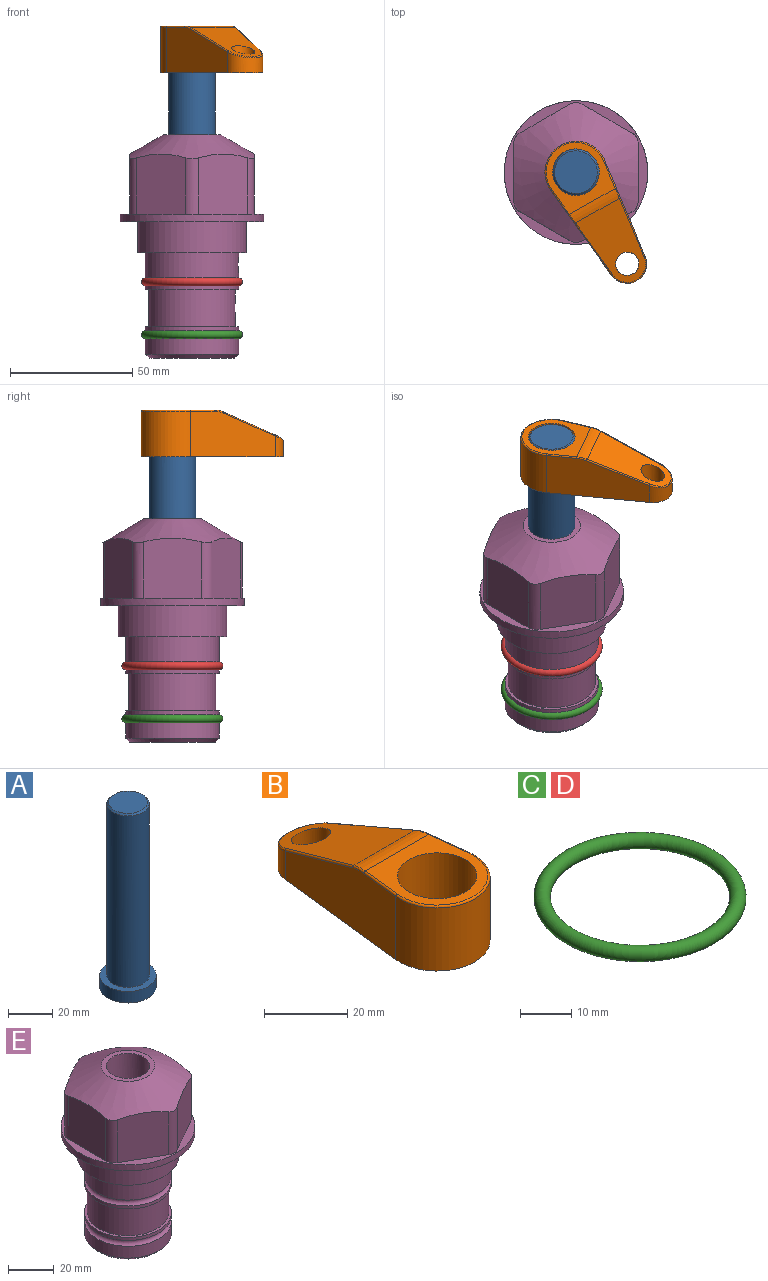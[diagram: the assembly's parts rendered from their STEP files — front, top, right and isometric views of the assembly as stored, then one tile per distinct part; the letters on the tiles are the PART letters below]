
ASSEMBLY  parts=5 mates=3
PART A: 6 faces, bbox 25.4x25.4x101.6 mm
  f0: plane 17.46x17.46mm, normal (0,0,1), area 239.5mm2, adj f5
  f1: plane 25.4x25.4mm, normal (0,0,-1), area 506.7mm2, adj f2
  f2: cylinder r=12.7mm len=25.4mm, axis (0,0,1), area 506.7mm2, adj f1,f3
  f3: plane 25.4x25.4mm, normal (0,0,1), area 221.7mm2, adj f2,f4
  f4: cylinder r=9.53mm len=94.46mm, axis (0,0,1), area 5653mm2, adj f3,f5
  f5: cone r=8.73mm half-angle=45deg, axis (0,0,-1), area 64.4mm2, adj f0,f4
PART B: 44 faces, bbox 27.5x64.5x19.1 mm
  f0: plane 2.3x0.95mm, normal (0,0,-1), area 1mm2, adj f25,f30,f34
  f1: plane 63.5x25.4mm, normal (0,0,-1), area 561.7mm2, adj f2,f3,f4,f5,f6,f7,f19,f20
  f2: cylinder r=12.7mm len=25.4mm, axis (0,0,-1), area 792.2mm2, adj f1,f3,f5,f13
  f3: plane 42.33x18.54mm, normal (0.99,0.11,0), area 647mm2, adj f1,f2,f4,f11,f12,f14
  f4: cylinder r=7.94mm len=15.78mm, axis (0,0,-1), area 158.6mm2, adj f1,f3,f5,f16
  f5: plane 42.33x18.54mm, normal (-0.99,0.11,0), area 647mm2, adj f1,f2,f4,f15,f17,f18
  f6: cylinder r=9.53mm len=19.05mm, axis (0,0,-1), area 1140.1mm2, adj f1,f8
  f7: cylinder r=4.76mm len=10.98mm, axis (0,0,-1), area 276.1mm2, adj f1,f9
  f8: plane 25.83x24.38mm, normal (0,0,1), area 262.2mm2, adj f6,f10,f11,f13,f15
  f9: plane 32.49x20.55mm, normal (0,0.34,0.94), area 489.9mm2, adj f7,f10,f14,f16,f18
  f10: cylinder r=12.7mm len=21.49mm, axis (-1,0,0), area 93.2mm2, adj f8,f9,f12,f17
  f11: cylinder r=0.51mm len=12.34mm, axis (0.11,-0.99,0), area 9.9mm2, adj f3,f8,f12,f13
  f12: bspline ~7.62x1.64mm, area 3.5mm2, adj f3,f10,f11,f14
  f13: torus R=12.19mm, axis (0,0,1), area 33.6mm2, adj f2,f8,f11,f15
  f14: cylinder r=0.51mm len=26.01mm, axis (0.1,-0.93,0.34), area 21.6mm2, adj f3,f9,f12,f16
  f15: cylinder r=0.51mm len=12.34mm, axis (0.11,0.99,0), area 9.9mm2, adj f5,f8,f13,f17
  f16: bspline ~15.78x7.05mm, area 15.7mm2, adj f4,f9,f14,f18
  f17: bspline ~7.62x1.64mm, area 3.5mm2, adj f5,f10,f15,f18
  f18: cylinder r=0.51mm len=26.01mm, axis (0.1,0.93,-0.34), area 21.6mm2, adj f5,f9,f16,f17
  f19: plane 21.6x14.29mm, normal (-0.99,-0.11,0), area 242.6mm2, adj f1,f26,f28,f34,f36,f38
  f20: plane 21.6x14.29mm, normal (0.99,-0.11,0), area 242.6mm2, adj f1,f27,f29,f37,f39,f41
  f21: cylinder r=12.7mm len=14.29mm, axis (0,0,-1), area 173.2mm2, adj f1,f26,f27,f30,f31,f33
  f22: cylinder r=7.94mm len=7.63mm, axis (0,0,-1), area 53.8mm2, adj f1,f28,f29,f42
  f23: plane 2.3x0.95mm, normal (0,0,-1), area 1mm2, adj f25,f33,f37
  f24: plane 17.94x12.32mm, normal (0,-0.34,-0.94), area 191.2mm2, adj f25,f38,f41,f42
  f25: cylinder r=9.53mm len=12.93mm, axis (-1,0,0), area 37.5mm2, adj f0,f23,f24,f31,f36,f39
  f26: cylinder r=1.59mm len=14.29mm, axis (0,0,-1), area 49mm2, adj f1,f19,f21,f32
  f27: cylinder r=1.59mm len=14.29mm, axis (0,0,-1), area 49mm2, adj f1,f20,f21,f35
  f28: cylinder r=1.59mm len=7.28mm, axis (0,0,-1), area 22.1mm2, adj f1,f19,f22,f40
  f29: cylinder r=1.59mm len=7.28mm, axis (0,0,-1), area 22.1mm2, adj f1,f20,f22,f43
  f30: torus R=14.29mm, axis (0,0,1), area 5.8mm2, adj f0,f21,f31,f32
  f31: bspline ~11.06x2.73mm, area 20.8mm2, adj f21,f25,f30,f33
  f32: sphere r=1.59mm, area 5.4mm2, adj f26,f30,f34
  f33: torus R=14.29mm, axis (0,0,1), area 5.8mm2, adj f21,f23,f31,f35
  f34: cylinder r=1.59mm len=1.68mm, axis (-0.11,0.99,0), area 2.4mm2, adj f0,f19,f32,f36
  f35: sphere r=1.59mm, area 5.4mm2, adj f27,f33,f37
  f36: bspline ~5.82x2.33mm, area 7.7mm2, adj f19,f25,f34,f38
  f37: cylinder r=1.59mm len=1.68mm, axis (0.11,0.99,0), area 2.4mm2, adj f20,f23,f35,f39
  f38: cylinder r=1.59mm len=18.33mm, axis (0.1,-0.93,0.34), area 46.7mm2, adj f19,f24,f36,f40
  f39: bspline ~5.82x2.33mm, area 7.7mm2, adj f20,f25,f37,f41
  f40: sphere r=1.59mm, area 3.6mm2, adj f28,f38,f42
  f41: cylinder r=1.59mm len=18.33mm, axis (0.1,0.93,-0.34), area 46.7mm2, adj f20,f24,f39,f43
  f42: bspline ~8.31x1.84mm, area 15.3mm2, adj f22,f24,f40,f43
  f43: sphere r=1.59mm, area 3.6mm2, adj f29,f41,f42
PART C: 1 faces, bbox 44.7x44.7x3.2 mm
  f0: torus R=19.05mm, axis (0,0,1), area 1193.9mm2
PART D: same geometry as C
PART E: 36 faces, bbox 58.7x58.7x91.2 mm
  f0: cylinder r=17.78mm len=35.56mm, axis (0,0,1), area 1670.8mm2, adj f23,f24,f31
  f1: cylinder r=19.05mm len=38.1mm, axis (0,0,1), area 1191.9mm2, adj f26,f27,f30
  f2: plane 58.66x58.66mm, normal (0,0,-1), area 1150.6mm2, adj f3,f28
  f3: cylinder r=29.33mm len=58.66mm, axis (0,0,-1), area 585.1mm2, adj f2,f4
  f4: plane 58.66x58.66mm, normal (0,0,1), area 475.9mm2, adj f3,f5,f6,f7,f8,f9,f10,f11
  f5: plane 24.5x20.32mm, normal (-0.5,0.87,0), area 562.8mm2, adj f4,f15,f16,f17
  f6: plane 24.5x20.32mm, normal (0.5,0.87,0), area 562.8mm2, adj f4,f14,f15,f17
  f7: plane 24.5x23.48mm, normal (1,0,0), area 562.8mm2, adj f4,f13,f14,f17
  f8: plane 24.5x20.32mm, normal (0.5,-0.87,0), area 562.8mm2, adj f4,f12,f13,f17
  f9: plane 24.5x20.32mm, normal (-0.5,-0.87,0), area 562.8mm2, adj f4,f11,f12,f17
  f10: plane 24.5x23.48mm, normal (-1,0,0), area 562.8mm2, adj f4,f11,f16,f17
  f11: cylinder r=5.08mm len=23.01mm, axis (0,0,-1), area 121.2mm2, adj f4,f9,f10,f17
  f12: cylinder r=5.08mm len=23.01mm, axis (0,0,-1), area 121.2mm2, adj f4,f8,f9,f17
  f13: cylinder r=5.08mm len=23.01mm, axis (0,0,-1), area 121.2mm2, adj f4,f7,f8,f17
  f14: cylinder r=5.08mm len=23.01mm, axis (0,0,-1), area 121.2mm2, adj f4,f6,f7,f17
  f15: cylinder r=5.08mm len=23.01mm, axis (0,0,-1), area 121.2mm2, adj f4,f5,f6,f17
  f16: cylinder r=5.08mm len=23.01mm, axis (0,0,-1), area 121.2mm2, adj f4,f5,f10,f17
  f17: cone r=11.73mm half-angle=60deg, axis (0,0,-1), area 2071.8mm2, adj f5,f6,f7,f8,f9,f10,f11,f12
  f18: plane 23.46x23.46mm, normal (0,0,1), area 147.4mm2, adj f17,f35
  f19: plane 34.93x34.93mm, normal (0,0,-1), area 958mm2, adj f29
  f20: cylinder r=19.05mm len=38.1mm, axis (0,0,1), area 760.1mm2, adj f21,f29
  f21: torus R=19.05mm, axis (0,0,1), area 565.3mm2, adj f20,f22
  f22: cylinder r=19.05mm len=38.1mm, axis (0,0,1), area 190mm2, adj f21,f23
  f23: plane 38.1x38.1mm, normal (0,0,1), area 146.9mm2, adj f0,f22
  f24: plane 38.1x38.1mm, normal (0,0,-1), area 146.9mm2, adj f0,f25
  f25: cylinder r=19.05mm len=38.1mm, axis (0,0,1), area 190mm2, adj f24,f26
  f26: torus R=19.05mm, axis (0,0,1), area 565.3mm2, adj f1,f25
  f27: plane 44.45x44.45mm, normal (0,0,-1), area 411.7mm2, adj f1,f28
  f28: cylinder r=22.23mm len=44.45mm, axis (0,0,1), area 1773.5mm2, adj f2,f27
  f29: cone r=19.05mm half-angle=45deg, axis (0,0,1), area 257.5mm2, adj f19,f20
  f30: cylinder r=3.17mm len=6.75mm, axis (-1,0,0), area 128mm2, adj f1,f33
  f31: cylinder r=3.17mm len=6.35mm, axis (-1,0,0), area 102.5mm2, adj f0,f33
  f32: plane 25.4x25.4mm, normal (0,0,1), area 506.7mm2, adj f33
  f33: cylinder r=12.7mm len=66.42mm, axis (0,0,-1), area 5236.2mm2, adj f30,f31,f32,f34
  f34: cone r=9.53mm half-angle=30deg, axis (0,0,-1), area 443.4mm2, adj f33,f35
  f35: cylinder r=9.53mm len=19.05mm, axis (0,0,-1), area 849mm2, adj f18,f34
PLACE A rot(axis=(0,0,-1),60.8deg) t=(0,0,6.38)mm
PLACE B rot(axis=(0,0,-1),150.8deg) t=(0,0,60.99)mm
PLACE C t=(0,0,-21.59)mm
PLACE D at identity
PLACE E at identity fixed
MATE fastened C.f0 <-> E.f0  axis (0,0,1) through (0,0,-46.1)mm
MATE cylindrical A.f2 <-> E.f0  axis (0,0,1) through (0,0,32.01)mm
MATE fastened B.f2 <-> A.f2  axis (0,0,1) through (0,0,80.04)mm
